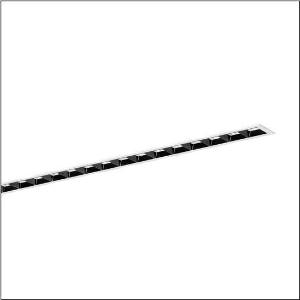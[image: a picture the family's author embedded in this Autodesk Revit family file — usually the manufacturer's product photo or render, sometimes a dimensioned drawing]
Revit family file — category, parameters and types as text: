
# Revit family: silica_r__21_51mx12db35wb_b505
name_source: partatom
category: Lighting Fixtures
units: mm (PartAtom-declared; Revit-internal decimal feet)

## family parameters
Cut with Voids When Loaded = No
Host = Face
Light Source = No
Part Type = Normal
Room Calculation Point = No
Round Connector Dimension = Use Diameter
Shared = No

## types (1)
- --- (1 x LED, 5400 lm, 34.3 W, 3000K)
    Apparent Load = 34 VA
    CIE Flux Codes = 86 100 100 100 100
    Color Rendering = 80
    Color Temperature = 3000K
    Default Elevation = 1800 mm
    Description = Silica® 21, office luminaire, primary light control with darklight reflector, of PMMA, black, CAT 2 (L<= 3000cd/m²), light emission: direct distribution, primary light characteristic: symmetric, installation type: recessed, LED, rated luminous flux: 5.400lm, luminous efficacy: 157lm/W, light colour: 830, colour temperature: 3000K, with terminal, 3+2-pole, max. 2.5mm², mains connection: 220..240V, AC, 50/60Hz, rated input power: 34.3W, luminaire housing, of aluminium, traffic white (RAL 9016), length: 1.528mm, width: 79mm, height: 53mm, protection rating (complete): IP20, insulation class (complete): insulation class I (protective earthing), certification: CE, permissible operating ambient temperature: 0..+35°C, standard: EN 50419, packaging unit: 1 piece
    Height = 0 mm  [stored 0 ft]
    Lamp = 1 x LED
    Lamp Light Flux = 5400 lm
    Lamp Power = 34.3 W
    Lamp count = 1
    Length = 1527 mm
    Luminous efficacy = 157 lm/W
    Manufacturer = Siteco
    ModVariant = No
    Model = 51MX12DB35WB
    Mounting Place = Ceiling
    Mounting Type = Recessed
    Number of Poles = 1
    OnlyDefault = Yes
    Power Factor = 1
    Product Name = Silica® 21
    Product group = office luminaire | ceiling recessed
    ProductGroupID = 401
    Protection Class = Protection class I
    Protection Degree = IP 20
    RLX_Detail_Level = 1
    RLX_Emergency_Light_Flux = 0 lm
    RLX_Emergency_Type = 0
    RLX_Emergency_Type_DB = No
    RlxData = <blob elided: 42097 chars, md5=ff255900>
    Socket = socket
    Standby Power = 0 W
    System Light Flux = 5400 lm
    System Power = 34 W
    Type Comments = factory setting: luminous flux: 100 % | dim-lin: 254 | 392 mA
    Type Image = l_1297791.jpg
    URL = http://relux.com
    VarID = @adj_055619
    Voltage = 0 V
    Weight = 0.00 kg
    Width = 79 mm

note: [stored X ft] marks values corroborated as IEEE doubles in the binary element streams (Revit-internal decimal feet)

## geometry (parser evidence)
native form markers: Blend x4, Sweep x11
no freeform markers — native parametric forms only
